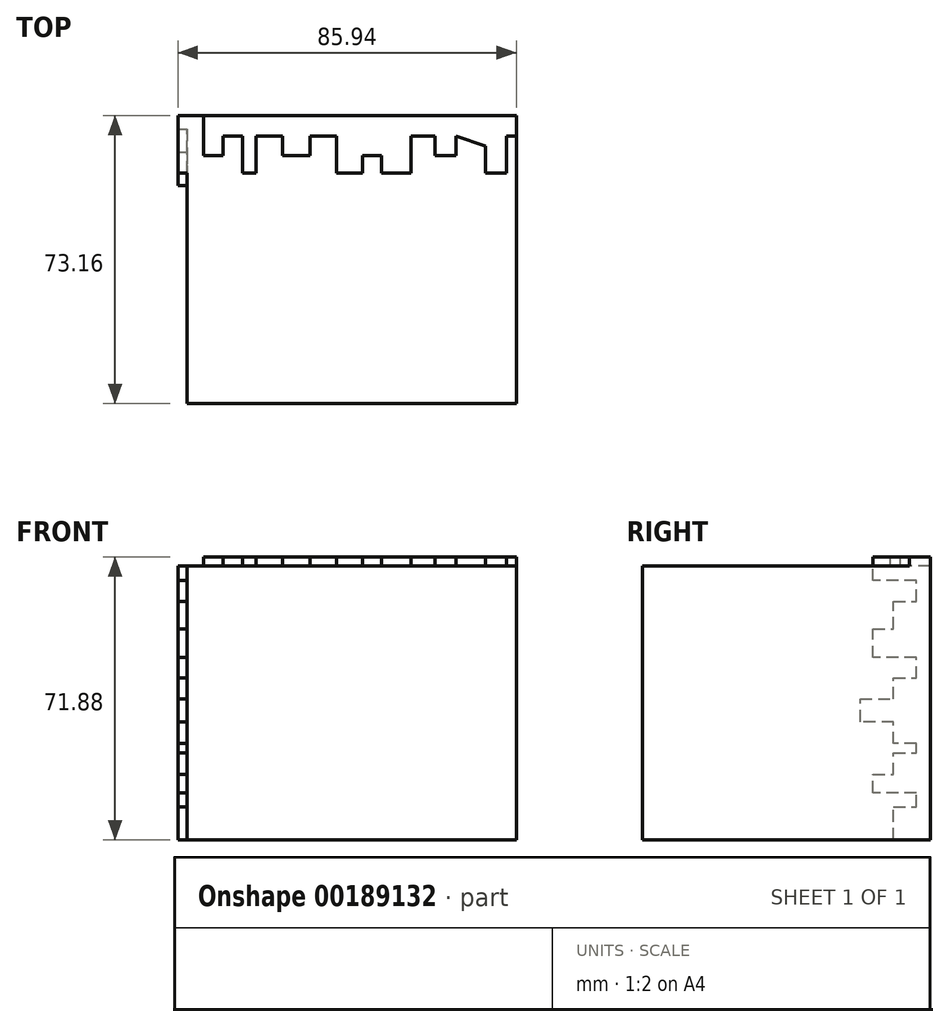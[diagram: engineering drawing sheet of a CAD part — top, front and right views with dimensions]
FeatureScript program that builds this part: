
annotation { "Feature Type Name" : "Feature", "Feature Type Description" : "" }
export const myFeature = defineFeature(function(context is Context, id is Id, definition is map)
    precondition{}
    {
        {
            var Q0;
            Q0=qCreatedBy(makeId("Top.planeOp"),FACE);
            var sketch = newSketch(context, id + "F0", { "sketchPlane" : qUnion([Q0])});
            skLineSegment(sketch, "E0.bottom", {"start": v(-44.6, 47.36) * mm, "end": v(39.06, 47.36) * mm});
            skLineSegment(sketch, "E0.top", {"start": v(-44.6, -25.8) * mm, "end": v(39.06, -25.8) * mm});
            skLineSegment(sketch, "E0.left", {"start": v(-44.6, 47.36) * mm, "end": v(-44.6, -25.8) * mm});
            skLineSegment(sketch, "E0.right", {"start": v(39.06, 47.36) * mm, "end": v(39.06, -25.8) * mm});
            skSolve(sketch);
        }
        {
            var Q0;
            Q0=makeQuery(id+"F0.imprint","IMPRINT",FACE,{"disambiguationData":[TD([[makeQuery(id+"F0.imprint","IMPRINT",EDGE,{"derivedFrom":sQuery(id+"F0.wireOp",EDGE,"E0.bottom")}),-1.0]])]});
            extrude(context, id + "F1", {"entities" : qUnion([Q0]), "depth" : 69.6 * mm});
        }
        {
            var Q0;
            Q0=makeQuery(id+"F1.opExtrude","SWEPT_FACE",FACE,{"disambiguationData":[OSD([sQuery(id+"F0.wireOp",EDGE,"E0.left")])]});
            var sketch = newSketch(context, id + "F2", { "sketchPlane" : qUnion([Q0])});
            skLineSegment(sketch, "E1", {"start": v(-38.04, 0) * mm, "end": v(-38.04, 8.45) * mm});
            skLineSegment(sketch, "E2", {"start": v(-38.04, 8.45) * mm, "end": v(-43.87, 8.45) * mm});
            skLineSegment(sketch, "E3", {"start": v(-43.87, 8.45) * mm, "end": v(-43.87, 11.95) * mm});
            skLineSegment(sketch, "E4", {"start": v(-43.87, 11.95) * mm, "end": v(-32.8, 11.95) * mm});
            skLineSegment(sketch, "E5", {"start": v(-32.8, 11.95) * mm, "end": v(-32.8, 16.61) * mm});
            skLineSegment(sketch, "E6", {"start": v(-32.8, 16.61) * mm, "end": v(-38.04, 16.61) * mm});
            skLineSegment(sketch, "E7", {"start": v(-38.04, 16.61) * mm, "end": v(-38.04, 22.15) * mm});
            skLineSegment(sketch, "E8", {"start": v(-38.04, 22.15) * mm, "end": v(-43.87, 22.15) * mm});
            skLineSegment(sketch, "E9", {"start": v(-43.87, 22.15) * mm, "end": v(-43.87, 24.48) * mm});
            skLineSegment(sketch, "E10", {"start": v(-43.87, 24.48) * mm, "end": v(-38.04, 24.48) * mm});
            skLineSegment(sketch, "E11", {"start": v(-38.04, 24.48) * mm, "end": v(-38.04, 30.02) * mm});
            skLineSegment(sketch, "E12", {"start": v(-38.04, 30.02) * mm, "end": v(-29.58, 30.02) * mm});
            skLineSegment(sketch, "E13", {"start": v(-29.58, 30.02) * mm, "end": v(-29.58, 35.85) * mm});
            skLineSegment(sketch, "E14", {"start": v(-29.58, 35.85) * mm, "end": v(-38.04, 35.85) * mm});
            skLineSegment(sketch, "E15", {"start": v(-38.04, 35.85) * mm, "end": v(-38.04, 41.1) * mm});
            skLineSegment(sketch, "E16", {"start": v(-38.04, 41.1) * mm, "end": v(-43.87, 41.1) * mm});
            skLineSegment(sketch, "E17", {"start": v(-43.87, 41.1) * mm, "end": v(-43.87, 46.34) * mm});
            skLineSegment(sketch, "E18", {"start": v(-43.87, 46.34) * mm, "end": v(-32.8, 46.34) * mm});
            skLineSegment(sketch, "E19", {"start": v(-32.8, 46.34) * mm, "end": v(-32.8, 53.63) * mm});
            skLineSegment(sketch, "E20", {"start": v(-32.8, 53.63) * mm, "end": v(-38.04, 53.63) * mm});
            skLineSegment(sketch, "E21", {"start": v(-38.04, 53.63) * mm, "end": v(-38.04, 60.63) * mm});
            skLineSegment(sketch, "E22", {"start": v(-38.04, 60.63) * mm, "end": v(-43.87, 60.63) * mm});
            skLineSegment(sketch, "E23", {"start": v(-43.87, 60.63) * mm, "end": v(-43.87, 65.87) * mm});
            skLineSegment(sketch, "E24", {"start": v(-43.87, 65.87) * mm, "end": v(-32.8, 65.87) * mm});
            skLineSegment(sketch, "E25", {"start": v(-32.8, 65.87) * mm, "end": v(-32.8, 69.6) * mm});
            skLineSegment(sketch, "E26", {"start": v(-32.8, 69.6) * mm, "end": v(-47.36, 69.6) * mm});
            skLineSegment(sketch, "E27", {"start": v(-47.36, 69.6) * mm, "end": v(-47.36, 0) * mm});
            skLineSegment(sketch, "E28", {"start": v(-47.36, 0) * mm, "end": v(-38.04, 0) * mm});
            skSolve(sketch);
        }
        {
            var Q0;
            Q0=makeQuery(id+"F2.imprint","IMPRINT",FACE,{"disambiguationData":[TD([[makeQuery(id+"F2.imprint","IMPRINT",EDGE,{"derivedFrom":sQuery(id+"F2.wireOp",EDGE,"E1")}),1.0]])]});
            extrude(context, id + "F3", {"entities" : qUnion([Q0]), "operationType" : NewBodyOperationType.ADD, "depth" : 2.3 * mm});
        }
        {
            var Q0;
            Q0=makeQuery(id+"F3.boolean.opBoolean","MERGE",FACE,{"derivedFrom":[makeQuery(id+"F1.opExtrude","CAP_FACE",FACE,{"disambiguationData":[OSD([sQuery(id+"F0.wireOp",EDGE,"E0.bottom"),sQuery(id+"F0.wireOp",EDGE,"E0.top"),sQuery(id+"F0.wireOp",EDGE,"E0.left"),sQuery(id+"F0.wireOp",EDGE,"E0.right")])],"isStart":false}),makeQuery(id+"F3.opExtrude","SWEPT_FACE",FACE,{"disambiguationData":[OSD([sQuery(id+"F2.wireOp",EDGE,"E26")])]})]});
            var sketch = newSketch(context, id + "F4", { "sketchPlane" : qUnion([Q0])});
            skLineSegment(sketch, "E29", {"start": v(-40.41, 47.36) * mm, "end": v(-40.41, 37.16) * mm});
            skLineSegment(sketch, "E30", {"start": v(-40.41, 37.16) * mm, "end": v(-35.46, 37.16) * mm});
            skLineSegment(sketch, "E31", {"start": v(-35.46, 37.16) * mm, "end": v(-35.46, 42.12) * mm});
            skLineSegment(sketch, "E32", {"start": v(-35.46, 42.12) * mm, "end": v(-30.5, 42.12) * mm});
            skLineSegment(sketch, "E33", {"start": v(-30.5, 42.12) * mm, "end": v(-30.5, 32.8) * mm});
            skLineSegment(sketch, "E34", {"start": v(-30.5, 32.8) * mm, "end": v(-27, 32.8) * mm});
            skLineSegment(sketch, "E35", {"start": v(-27, 32.8) * mm, "end": v(-27, 42.12) * mm});
            skLineSegment(sketch, "E36", {"start": v(-27, 42.12) * mm, "end": v(-20.3, 42.12) * mm});
            skLineSegment(sketch, "E37", {"start": v(-20.3, 42.12) * mm, "end": v(-20.3, 37.16) * mm});
            skLineSegment(sketch, "E38", {"start": v(-20.3, 37.16) * mm, "end": v(-13.3, 37.16) * mm});
            skLineSegment(sketch, "E39", {"start": v(-13.3, 37.16) * mm, "end": v(-13.3, 42.12) * mm});
            skLineSegment(sketch, "E40", {"start": v(-13.3, 42.12) * mm, "end": v(-6.6, 42.12) * mm});
            skLineSegment(sketch, "E41", {"start": v(-6.6, 42.12) * mm, "end": v(-6.6, 32.8) * mm});
            skLineSegment(sketch, "E42", {"start": v(-6.6, 32.8) * mm, "end": v(0, 32.8) * mm});
            skLineSegment(sketch, "E43", {"start": v(0, 32.8) * mm, "end": v(0, 37.16) * mm});
            skLineSegment(sketch, "E44", {"start": v(0, 37.16) * mm, "end": v(4.77, 37.16) * mm});
            skLineSegment(sketch, "E45", {"start": v(4.77, 37.16) * mm, "end": v(4.77, 32.8) * mm});
            skLineSegment(sketch, "E46", {"start": v(4.77, 32.8) * mm, "end": v(12.35, 32.8) * mm});
            skLineSegment(sketch, "E47", {"start": v(12.35, 32.8) * mm, "end": v(12.35, 42.12) * mm});
            skLineSegment(sketch, "E48", {"start": v(12.35, 42.12) * mm, "end": v(18.47, 42.12) * mm});
            skLineSegment(sketch, "E49", {"start": v(18.47, 42.12) * mm, "end": v(18.47, 37.16) * mm});
            skLineSegment(sketch, "E50", {"start": v(18.47, 37.16) * mm, "end": v(23.71, 37.16) * mm});
            skLineSegment(sketch, "E51", {"start": v(23.71, 37.16) * mm, "end": v(23.71, 42.12) * mm});
            skLineSegment(sketch, "E52", {"start": v(23.71, 42.12) * mm, "end": v(31.3, 39.64) * mm});
            skPoint(sketch, "E52.endSnap0", {"position": v(23.71, 39.64) * mm});
            skLineSegment(sketch, "E53", {"start": v(31.3, 39.64) * mm, "end": v(31.3, 32.8) * mm});
            skLineSegment(sketch, "E54", {"start": v(31.3, 32.8) * mm, "end": v(36.54, 32.8) * mm});
            skLineSegment(sketch, "E55", {"start": v(36.54, 32.8) * mm, "end": v(36.54, 42.12) * mm});
            skLineSegment(sketch, "E56", {"start": v(36.54, 42.12) * mm, "end": v(39.06, 42.12) * mm});
            skLineSegment(sketch, "E57", {"start": v(39.06, 42.12) * mm, "end": v(39.06, 47.36) * mm});
            skLineSegment(sketch, "E58", {"start": v(39.06, 47.36) * mm, "end": v(-46.88, 47.36) * mm});
            skLineSegment(sketch, "E59", {"start": v(-46.88, 47.36) * mm, "end": v(-46.88, 37.16) * mm});
            skLineSegment(sketch, "E60", {"start": v(-46.88, 37.16) * mm, "end": v(-40.41, 37.16) * mm});
            skSolve(sketch);
        }
        {
            var Q0;
            {var subQ0=sQuery(id+"F4.wireOp",EDGE,"E29");Q0=makeQuery(id+"F4.imprint","IMPRINT",FACE,{"disambiguationData":[TD([[makeQuery(id+"F4.imprint","IMPRINT",EDGE,{"derivedFrom":subQ0}),1.0]])]});}
            extrude(context, id + "F5", {"entities" : qUnion([Q0]), "operationType" : NewBodyOperationType.ADD, "depth" : 2.3 * mm});
        }
    });
